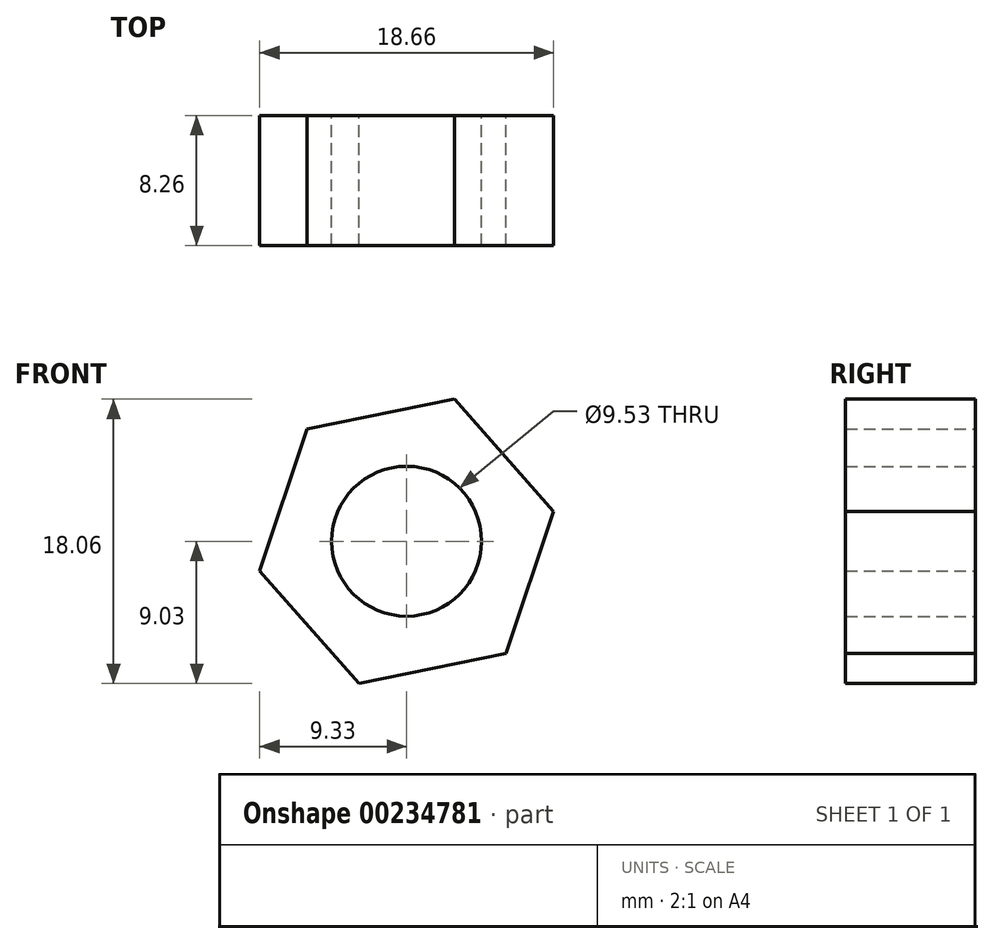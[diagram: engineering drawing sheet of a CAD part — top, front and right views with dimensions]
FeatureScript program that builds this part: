
annotation { "Feature Type Name" : "Feature", "Feature Type Description" : "" }
export const myFeature = defineFeature(function(context is Context, id is Id, definition is map)
    precondition{}
    {
        {
            var Q0;
            Q0=qCreatedBy(makeId("Front.planeOp"),FACE);
            var sketch = newSketch(context, id + "F1", { "sketchPlane" : qUnion([Q0])});
            skCircle(sketch, "E0.cCircle", {"center": v(0, 0) * mm, "radius": 9.52 * mm, "construction": true});
            skLineSegment(sketch, "E0.0", {"start": v(6.3, -7.14) * mm, "end": v(-3.03, -9.03) * mm});
            skLineSegment(sketch, "E0.1", {"start": v(-3.03, -9.03) * mm, "end": v(-9.33, -1.9) * mm});
            skLineSegment(sketch, "E0.2", {"start": v(-9.33, -1.9) * mm, "end": v(-6.3, 7.14) * mm});
            skLineSegment(sketch, "E0.3", {"start": v(-6.3, 7.14) * mm, "end": v(3.03, 9.03) * mm});
            skLineSegment(sketch, "E0.4", {"start": v(3.03, 9.03) * mm, "end": v(9.33, 1.9) * mm});
            skLineSegment(sketch, "E0.5", {"start": v(9.33, 1.9) * mm, "end": v(6.3, -7.14) * mm});
            skCircle(sketch, "E1", {"center": v(0, 0) * mm, "radius": 4.76 * mm});
            skSolve(sketch);
        }
        {
            var Q0;
            Q0=makeQuery(id+"F1.imprint","IMPRINT",FACE,{"disambiguationData":[TD([[makeQuery(id+"F1.imprint","IMPRINT",EDGE,{"derivedFrom":sQuery(id+"F1.wireOp",EDGE,"E0.0")}),-1.0]])]});
            extrude(context, id + "F0", {"entities" : qUnion([Q0]), "depth" : 8.25 * mm});
        }
    });
